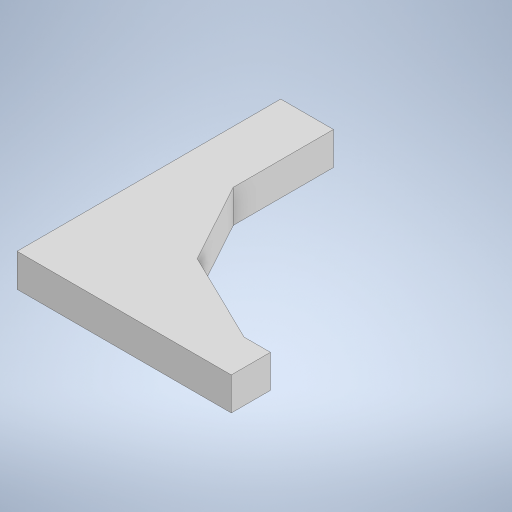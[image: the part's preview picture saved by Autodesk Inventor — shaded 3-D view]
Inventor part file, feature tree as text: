
AUTODESK INVENTOR PART (.ipt)
format: ipt  version: 2024 (Build 280153000, 153)  size: 230,400 bytes
history: native  units: mm
features: extrude x1, sketch x1
ambient origin geometry x8: Origin, YZ Plane, XZ Plane, XY Plane, X Axis, Y Axis, Z Axis, Center Point
bodies: Solid1 (feature_tree)
feature tree (2):
  extrude  "Extrusion1"  Depth=80.0mm
  sketch  "Sketch1"  dims[d0=65.0mm d1=80.0mm d3=10.0mm d4=0.0mm d5=16.0mm d6=52.4mm]
